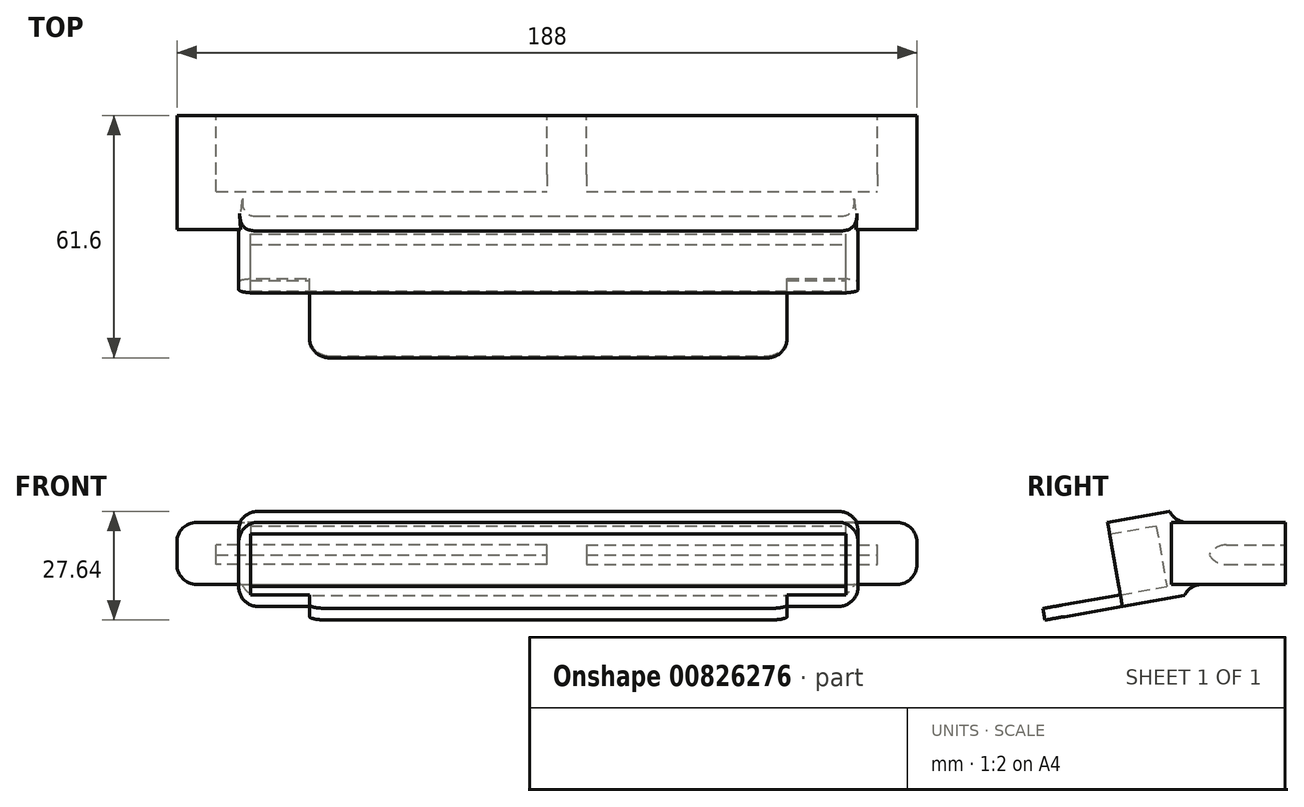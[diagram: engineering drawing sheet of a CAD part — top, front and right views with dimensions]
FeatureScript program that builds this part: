
annotation { "Feature Type Name" : "Feature", "Feature Type Description" : "" }
export const myFeature = defineFeature(function(context is Context, id is Id, definition is map)
    precondition{}
    {
        {
            var Q0;
            Q0=qCreatedBy(makeId("Front.planeOp"),FACE);
            var sketch = newSketch(context, id + "F0", { "sketchPlane" : qUnion([Q0])});
            skLineSegment(sketch, "E0.bottom", {"start": v(-71.26, -2.8) * mm, "end": v(80.06, -2.8) * mm});
            skLineSegment(sketch, "E0.top", {"start": v(-71.26, -18.5) * mm, "end": v(80.06, -18.5) * mm});
            skLineSegment(sketch, "E0.left", {"start": v(-71.26, -2.8) * mm, "end": v(-71.26, -18.5) * mm});
            skLineSegment(sketch, "E0.right", {"start": v(80.06, -2.8) * mm, "end": v(80.06, -18.5) * mm});
            skLineSegment(sketch, "E1.bottom", {"start": v(-74.26, 0.2) * mm, "end": v(83.06, 0.2) * mm});
            skLineSegment(sketch, "E1.top", {"start": v(-74.26, -21.5) * mm, "end": v(83.06, -21.5) * mm});
            skLineSegment(sketch, "E1.left", {"start": v(-74.26, 0.2) * mm, "end": v(-74.26, -21.5) * mm});
            skLineSegment(sketch, "E1.right", {"start": v(83.06, 0.2) * mm, "end": v(83.06, -21.5) * mm});
            skSolve(sketch);
        }
        {
            var Q0;
            Q0 = qSketchRegion(id + "F0", true);
            extrude(context, id + "F1", {"entities" : qUnion([Q0]), "depth" : 12 * mm, "offsetDistance" : 25 * mm});
        }
        {
            var Q0;
            Q0=makeQuery(id+"F0.imprint","IMPRINT",FACE,{"disambiguationData":[TD([[makeQuery(id+"F0.imprint","IMPRINT",EDGE,{"derivedFrom":sQuery(id+"F0.wireOp",EDGE,"E0.bottom")}),1.0]])]});
            var Q1;
            Q1=makeQuery(id+"F0.imprint","IMPRINT",FACE,{"disambiguationData":[TD([[makeQuery(id+"F0.imprint","IMPRINT",EDGE,{"derivedFrom":sQuery(id+"F0.wireOp",EDGE,"E0.bottom")}),-1.0]])]});
            extrude(context, id + "F2", {"entities" : qUnion([Q0, Q1]), "operationType" : NewBodyOperationType.ADD, "oppositeDirection" : true, "depth" : 4 * mm, "offsetDistance" : 25 * mm});
        }
        {
            var Q0;
            {var subQ0=sQuery(id+"F0.wireOp",EDGE,"E1.left");var subQ1=sQuery(id+"F0.wireOp",EDGE,"E1.top");Q0=makeQuery(id+"F2.boolean.opBoolean","MERGE",EDGE,{"derivedFrom":[makeQuery(id+"F1.opExtrude","SWEPT_EDGE",EDGE,{"disambiguationData":[OSD([subQ1,subQ0])]}),makeQuery(id+"F2.opExtrude","SWEPT_EDGE",EDGE,{"disambiguationData":[OSD([subQ1,subQ0])]})]});}
            var Q1;
            {var subQ0=sQuery(id+"F0.wireOp",EDGE,"E1.left");var subQ1=sQuery(id+"F0.wireOp",EDGE,"E1.bottom");Q1=makeQuery(id+"F2.boolean.opBoolean","MERGE",EDGE,{"derivedFrom":[makeQuery(id+"F1.opExtrude","SWEPT_EDGE",EDGE,{"disambiguationData":[OSD([subQ1,subQ0])]}),makeQuery(id+"F2.opExtrude","SWEPT_EDGE",EDGE,{"disambiguationData":[OSD([subQ1,subQ0])]})]});}
            var Q2;
            {var subQ0=sQuery(id+"F0.wireOp",EDGE,"E1.right");var subQ1=sQuery(id+"F0.wireOp",EDGE,"E1.top");Q2=makeQuery(id+"F2.boolean.opBoolean","MERGE",EDGE,{"derivedFrom":[makeQuery(id+"F1.opExtrude","SWEPT_EDGE",EDGE,{"disambiguationData":[OSD([subQ1,subQ0])]}),makeQuery(id+"F2.opExtrude","SWEPT_EDGE",EDGE,{"disambiguationData":[OSD([subQ1,subQ0])]})]});}
            var Q3;
            {var subQ0=sQuery(id+"F0.wireOp",EDGE,"E1.right");var subQ1=sQuery(id+"F0.wireOp",EDGE,"E1.bottom");Q3=makeQuery(id+"F2.boolean.opBoolean","MERGE",EDGE,{"derivedFrom":[makeQuery(id+"F1.opExtrude","SWEPT_EDGE",EDGE,{"disambiguationData":[OSD([subQ1,subQ0])]}),makeQuery(id+"F2.opExtrude","SWEPT_EDGE",EDGE,{"disambiguationData":[OSD([subQ1,subQ0])]})]});}
            fillet(context, id + "F3", {"entities" : qUnion([Q0, Q1, Q2, Q3]), "radius" : 5 * mm, "tangentPropagation" : true, "allowEdgeOverflow" : false});
        }
        {
            var Q0;
            Q0=qCreatedBy(makeId("Front.planeOp"),FACE);
            var sketch = newSketch(context, id + "F4", { "sketchPlane" : qUnion([Q0])});
            skLineSegment(sketch, "E2.bottom", {"start": v(-2.96, -39.43) * mm, "end": v(185.04, -39.43) * mm});
            skLineSegment(sketch, "E2.top", {"start": v(-2.96, -23.71) * mm, "end": v(185.04, -23.71) * mm});
            skLineSegment(sketch, "E2.left", {"start": v(-2.96, -39.43) * mm, "end": v(-2.96, -23.71) * mm});
            skLineSegment(sketch, "E2.right", {"start": v(185.04, -39.43) * mm, "end": v(185.04, -23.71) * mm});
            skPoint(sketch, "E2.middle", {"position": v(91.04, -31.57) * mm});
            skSolve(sketch);
        }
        {
            var Q0;
            Q0 = qSketchRegion(id + "F4", true);
            extrude(context, id + "F5", {"entities" : qUnion([Q0]), "depth" : -29 * mm, "offsetDistance" : 25 * mm});
        }
        {
            var Q0;
            Q0=makeQuery(id+"F5.opExtrude","SWEPT_BODY",BODY,{"disambiguationData":[OSD([sQuery(id+"F4.wireOp",EDGE,"E2.bottom"),sQuery(id+"F4.wireOp",EDGE,"E2.top"),sQuery(id+"F4.wireOp",EDGE,"E2.left"),sQuery(id+"F4.wireOp",EDGE,"E2.right")])]});
            transform(context, id + "F6", {"entities" : qUnion([Q0]), "transformType" : TransformType.TRANSLATION_3D, "dx" : -85.6 * mm, "dy" : 0 * mm, "dz" : 21.1 * mm, "makeCopy" : false});
        }
        {
            var Q0;
            Q0=makeQuery(id+"F5.opExtrude","SWEPT_BODY",BODY,{"disambiguationData":[OSD([sQuery(id+"F4.wireOp",EDGE,"E2.bottom"),sQuery(id+"F4.wireOp",EDGE,"E2.top"),sQuery(id+"F4.wireOp",EDGE,"E2.left"),sQuery(id+"F4.wireOp",EDGE,"E2.right")])]});
            transform(context, id + "F7", {"entities" : qUnion([Q0]), "transformType" : TransformType.TRANSLATION_3D, "dx" : 0 * mm, "dy" : 0.4 * mm, "dz" : 0 * mm, "makeCopy" : false});
        }
        {
            var Q0;
            Q0=makeQuery(id+"F1.opExtrude","SWEPT_BODY",BODY,{"disambiguationData":[OSD([sQuery(id+"F0.wireOp",EDGE,"E0.bottom"),sQuery(id+"F0.wireOp",EDGE,"E0.top"),sQuery(id+"F0.wireOp",EDGE,"E0.left"),sQuery(id+"F0.wireOp",EDGE,"E0.right"),sQuery(id+"F0.wireOp",EDGE,"E1.bottom"),sQuery(id+"F0.wireOp",EDGE,"E1.top"),sQuery(id+"F0.wireOp",EDGE,"E1.left"),sQuery(id+"F0.wireOp",EDGE,"E1.right")])]});
            transform(context, id + "F8", {"entities" : qUnion([Q0]), "transformType" : TransformType.TRANSLATION_3D, "dx" : 1.4 * mm, "dy" : 0 * mm, "dz" : 0 * mm, "makeCopy" : false});
        }
        {
            var Q0;
            Q0=makeQuery(id+"F1.opExtrude","SWEPT_BODY",BODY,{"disambiguationData":[OSD([sQuery(id+"F0.wireOp",EDGE,"E0.bottom"),sQuery(id+"F0.wireOp",EDGE,"E0.top"),sQuery(id+"F0.wireOp",EDGE,"E0.left"),sQuery(id+"F0.wireOp",EDGE,"E0.right"),sQuery(id+"F0.wireOp",EDGE,"E1.bottom"),sQuery(id+"F0.wireOp",EDGE,"E1.top"),sQuery(id+"F0.wireOp",EDGE,"E1.left"),sQuery(id+"F0.wireOp",EDGE,"E1.right")])]});
            var Q1;
            Q1=makeQuery(id+"F2.opExtrude","CAP_EDGE",EDGE,{"disambiguationData":[OSD([sQuery(id+"F0.wireOp",EDGE,"E1.bottom")])],"isStart":false});
            transform(context, id + "F9", {"entities" : qUnion([Q0]), "transformType" : TransformType.ROTATION, "transformAxis" : qUnion([Q1]), "angle" : 10 * degree, "makeCopy" : false});
        }
        {
            var Q0;
            Q0=makeQuery(id+"F1.opExtrude","SWEPT_BODY",BODY,{"disambiguationData":[OSD([sQuery(id+"F0.wireOp",EDGE,"E0.bottom"),sQuery(id+"F0.wireOp",EDGE,"E0.top"),sQuery(id+"F0.wireOp",EDGE,"E0.left"),sQuery(id+"F0.wireOp",EDGE,"E0.right"),sQuery(id+"F0.wireOp",EDGE,"E1.bottom"),sQuery(id+"F0.wireOp",EDGE,"E1.top"),sQuery(id+"F0.wireOp",EDGE,"E1.left"),sQuery(id+"F0.wireOp",EDGE,"E1.right")])]});
            transform(context, id + "F10", {"entities" : qUnion([Q0]), "transformType" : TransformType.TRANSLATION_3D, "dx" : 0 * mm, "dy" : -4 * mm, "dz" : 0 * mm, "makeCopy" : false});
        }
        {
            var Q0;
            Q0=makeQuery(id+"F1.opExtrude","CAP_FACE",FACE,{"disambiguationData":[OSD([sQuery(id+"F0.wireOp",EDGE,"E0.bottom"),sQuery(id+"F0.wireOp",EDGE,"E0.top"),sQuery(id+"F0.wireOp",EDGE,"E0.left"),sQuery(id+"F0.wireOp",EDGE,"E0.right"),sQuery(id+"F0.wireOp",EDGE,"E1.bottom"),sQuery(id+"F0.wireOp",EDGE,"E1.top"),sQuery(id+"F0.wireOp",EDGE,"E1.left"),sQuery(id+"F0.wireOp",EDGE,"E1.right")])],"isStart":false});
            var sketch = newSketch(context, id + "F11", { "sketchPlane" : qUnion([Q0])});
            skLineSegment(sketch, "E3.bottom", {"start": v(-54.86, -18.5) * mm, "end": v(66.46, -18.5) * mm});
            skLineSegment(sketch, "E3.top", {"start": v(-54.86, -21.5) * mm, "end": v(66.46, -21.5) * mm});
            skLineSegment(sketch, "E3.left", {"start": v(-54.86, -18.5) * mm, "end": v(-54.86, -21.5) * mm});
            skLineSegment(sketch, "E3.right", {"start": v(66.46, -18.5) * mm, "end": v(66.46, -21.5) * mm});
            skSolve(sketch);
        }
        {
            var Q0;
            Q0 = qSketchRegion(id + "F11", true);
            extrude(context, id + "F12", {"entities" : qUnion([Q0]), "operationType" : NewBodyOperationType.ADD, "depth" : 20 * mm, "offsetDistance" : 25 * mm});
        }
        {
            var Q0;
            Q0=makeQuery(id+"F12.opExtrude","CAP_EDGE",EDGE,{"disambiguationData":[OSD([sQuery(id+"F11.wireOp",EDGE,"E3.left")])],"isStart":false});
            var Q1;
            Q1=makeQuery(id+"F12.opExtrude","CAP_EDGE",EDGE,{"disambiguationData":[OSD([sQuery(id+"F11.wireOp",EDGE,"E3.right")])],"isStart":false});
            fillet(context, id + "F13", {"entities" : qUnion([Q0, Q1]), "radius" : 5 * mm, "tangentPropagation" : true, "allowEdgeOverflow" : false});
        }
        {
            var Q0;
            Q0=makeQuery(id+"F5.opExtrude","CAP_FACE",FACE,{"disambiguationData":[OSD([sQuery(id+"F4.wireOp",EDGE,"E2.bottom"),sQuery(id+"F4.wireOp",EDGE,"E2.top"),sQuery(id+"F4.wireOp",EDGE,"E2.left"),sQuery(id+"F4.wireOp",EDGE,"E2.right")])],"isStart":false});
            var sketch = newSketch(context, id + "F14", { "sketchPlane" : qUnion([Q0])});
            skLineSegment(sketch, "E4.bottom", {"start": v(-15.44, -13.33) * mm, "end": v(-89.44, -13.33) * mm});
            skLineSegment(sketch, "E4.top", {"start": v(-15.44, -8.33) * mm, "end": v(-89.44, -8.33) * mm});
            skLineSegment(sketch, "E4.left", {"start": v(-5.44, -13.33) * mm, "end": v(-5.44, -8.33) * mm});
            skLineSegment(sketch, "E4.right", {"start": v(-89.44, -13.33) * mm, "end": v(-89.44, -8.33) * mm});
            skPoint(sketch, "E4.middle", {"position": v(-47.44, -10.83) * mm});
            skLineSegment(sketch, "E5.MirrorCS", {"start": v(-5.44, -8.33) * mm, "end": v(78.56, -8.33) * mm});
            skLineSegment(sketch, "E6.MirrorCS", {"start": v(78.56, -13.33) * mm, "end": v(78.56, -8.33) * mm});
            skLineSegment(sketch, "E7.MirrorCS", {"start": v(-5.44, -13.33) * mm, "end": v(78.56, -13.33) * mm});
            skLineSegment(sketch, "E8", {"start": v(-15.44, -8.33) * mm, "end": v(-15.44, -13.33) * mm});
            skSolve(sketch);
        }
        {
            var Q0;
            Q0 = qSketchRegion(id + "F14", true);
            extrude(context, id + "F15", {"entities" : qUnion([Q0]), "operationType" : NewBodyOperationType.REMOVE, "oppositeDirection" : true, "depth" : 20 * mm, "offsetDistance" : 25 * mm});
        }
        {
            var Q0;
            Q0=makeQuery(id+"F5.opExtrude","SWEPT_EDGE",EDGE,{"disambiguationData":[OSD([sQuery(id+"F4.wireOp",EDGE,"E2.bottom"),sQuery(id+"F4.wireOp",EDGE,"E2.right")])]});
            var Q1;
            Q1=makeQuery(id+"F5.opExtrude","SWEPT_EDGE",EDGE,{"disambiguationData":[OSD([sQuery(id+"F4.wireOp",EDGE,"E2.top"),sQuery(id+"F4.wireOp",EDGE,"E2.right")])]});
            var Q2;
            Q2=makeQuery(id+"F5.opExtrude","SWEPT_EDGE",EDGE,{"disambiguationData":[OSD([sQuery(id+"F4.wireOp",EDGE,"E2.top"),sQuery(id+"F4.wireOp",EDGE,"E2.left")])]});
            var Q3;
            Q3=makeQuery(id+"F5.opExtrude","SWEPT_EDGE",EDGE,{"disambiguationData":[OSD([sQuery(id+"F4.wireOp",EDGE,"E2.bottom"),sQuery(id+"F4.wireOp",EDGE,"E2.left")])]});
            fillet(context, id + "F16", {"entities" : qUnion([Q0, Q1, Q2, Q3]), "radius" : 5 * mm, "tangentPropagation" : true, "allowEdgeOverflow" : false});
        }
        {
            var Q0;
            Q0=makeQuery(id+"F1.opExtrude","SWEPT_BODY",BODY,{"disambiguationData":[OSD([sQuery(id+"F0.wireOp",EDGE,"E0.bottom"),sQuery(id+"F0.wireOp",EDGE,"E0.top"),sQuery(id+"F0.wireOp",EDGE,"E0.left"),sQuery(id+"F0.wireOp",EDGE,"E0.right"),sQuery(id+"F0.wireOp",EDGE,"E1.bottom"),sQuery(id+"F0.wireOp",EDGE,"E1.top"),sQuery(id+"F0.wireOp",EDGE,"E1.left"),sQuery(id+"F0.wireOp",EDGE,"E1.right")])]});
            var Q1;
            Q1=makeQuery(id+"F5.opExtrude","SWEPT_BODY",BODY,{"disambiguationData":[OSD([sQuery(id+"F4.wireOp",EDGE,"E2.bottom"),sQuery(id+"F4.wireOp",EDGE,"E2.top"),sQuery(id+"F4.wireOp",EDGE,"E2.left"),sQuery(id+"F4.wireOp",EDGE,"E2.right")])]});
            booleanBodies(context, id + "F17", {"operationType" : BooleanOperationType.UNION, "tools" : qUnion([Q0, Q1])});
        }
        {
            var Q0;
            Q0=makeQuery(id+"F17.opBoolean","INTERSECT",EDGE,{"derivedFrom":[makeQuery(id+"F2.opExtrude","CAP_FACE",FACE,{"disambiguationData":[OSD([sQuery(id+"F0.wireOp",EDGE,"E1.bottom"),sQuery(id+"F0.wireOp",EDGE,"E1.top"),sQuery(id+"F0.wireOp",EDGE,"E1.left"),sQuery(id+"F0.wireOp",EDGE,"E1.right")])],"isStart":false}),makeQuery(id+"F5.opExtrude","SWEPT_FACE",FACE,{"disambiguationData":[OSD([sQuery(id+"F4.wireOp",EDGE,"E2.top")])]})]});
            fillet(context, id + "F18", {"entities" : qUnion([Q0]), "radius" : 5 * mm, "tangentPropagation" : true, "allowEdgeOverflow" : false});
        }
        {
            var Q0;
            Q0=makeQuery(id+"F17.opBoolean","INTERSECT",EDGE,{"derivedFrom":[makeQuery(id+"F2.opExtrude","CAP_FACE",FACE,{"disambiguationData":[OSD([sQuery(id+"F0.wireOp",EDGE,"E1.bottom"),sQuery(id+"F0.wireOp",EDGE,"E1.top"),sQuery(id+"F0.wireOp",EDGE,"E1.left"),sQuery(id+"F0.wireOp",EDGE,"E1.right")])],"isStart":false}),makeQuery(id+"F5.opExtrude","SWEPT_FACE",FACE,{"disambiguationData":[OSD([sQuery(id+"F4.wireOp",EDGE,"E2.bottom")])]})]});
            fillet(context, id + "F19", {"entities" : qUnion([Q0]), "radius" : 5 * mm, "tangentPropagation" : true, "allowEdgeOverflow" : false});
        }
        {
            var Q0;
            Q0=makeQuery(id+"F15.boolean.opBoolean","COPY",EDGE,{"derivedFrom":makeQuery(id+"F15.opExtrude","CAP_EDGE",EDGE,{"disambiguationData":[OSD([sQuery(id+"F14.wireOp",EDGE,"E4.top")])],"isStart":false})});
            var Q1;
            Q1=makeQuery(id+"F15.boolean.opBoolean","COPY",EDGE,{"derivedFrom":makeQuery(id+"F15.opExtrude","CAP_EDGE",EDGE,{"disambiguationData":[OSD([sQuery(id+"F14.wireOp",EDGE,"E4.bottom")])],"isStart":false})});
            var Q2;
            Q2=makeQuery(id+"F15.boolean.opBoolean","COPY",EDGE,{"derivedFrom":makeQuery(id+"F15.opExtrude","CAP_EDGE",EDGE,{"disambiguationData":[OSD([sQuery(id+"F14.wireOp",EDGE,"E5.MirrorCS")])],"isStart":false})});
            var Q3;
            Q3=makeQuery(id+"F15.boolean.opBoolean","COPY",EDGE,{"derivedFrom":makeQuery(id+"F15.opExtrude","CAP_EDGE",EDGE,{"disambiguationData":[OSD([sQuery(id+"F14.wireOp",EDGE,"E7.MirrorCS")])],"isStart":false})});
            fillet(context, id + "F20", {"entities" : qUnion([Q0, Q1, Q2, Q3]), "radius" : 5 * mm, "tangentPropagation" : true, "allowEdgeOverflow" : false});
        }
    });
